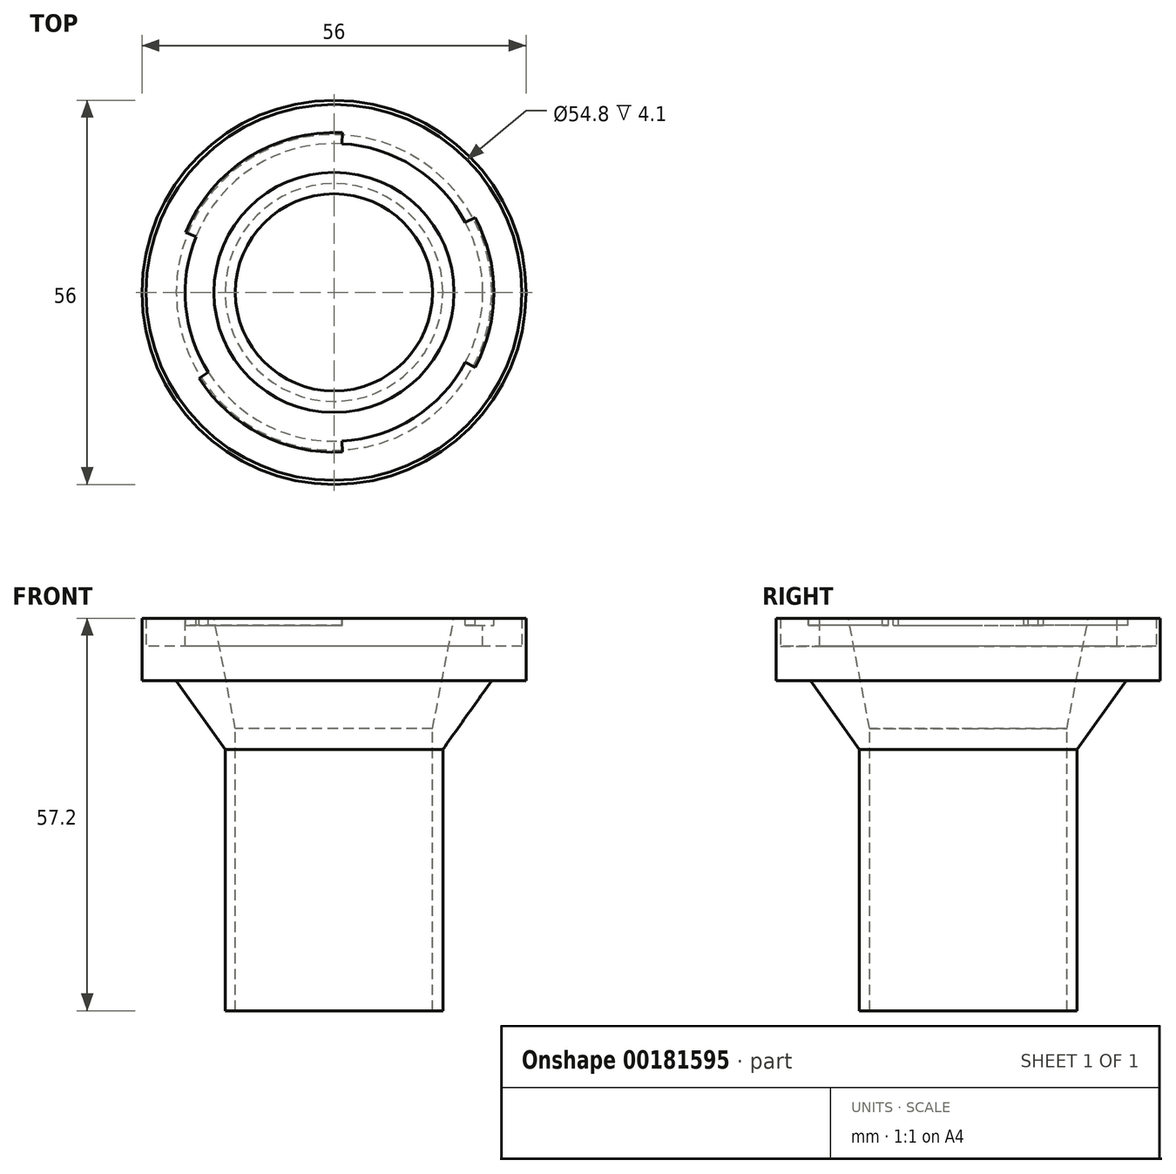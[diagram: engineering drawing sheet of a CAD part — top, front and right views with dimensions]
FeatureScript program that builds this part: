
annotation { "Feature Type Name" : "Feature", "Feature Type Description" : "" }
export const myFeature = defineFeature(function(context is Context, id is Id, definition is map)
    precondition{}
    {
        {
            var Q0;
            Q0=qCreatedBy(makeId("Front.planeOp"),FACE);
            var sketch = newSketch(context, id + "F0", { "sketchPlane" : qUnion([Q0])});
            skLineSegment(sketch, "E0", {"start": v(-17.5, 0) * mm, "end": v(-23.3, 0) * mm});
            skLineSegment(sketch, "E1", {"start": v(-23.3, 0) * mm, "end": v(-23.3, -1) * mm});
            skLineSegment(sketch, "E2", {"start": v(-23.3, -1) * mm, "end": v(-21.7, -1) * mm});
            skLineSegment(sketch, "E3", {"start": v(-21.7, -1) * mm, "end": v(-21.7, -4.1) * mm});
            skLineSegment(sketch, "E4", {"start": v(-21.7, -4.1) * mm, "end": v(-28, -4.1) * mm});
            skLineSegment(sketch, "E5", {"start": v(-28, -4.1) * mm, "end": v(-28, -9.1) * mm});
            skLineSegment(sketch, "E6", {"start": v(-28, -9.1) * mm, "end": v(-23, -9.1) * mm});
            skLineSegment(sketch, "E7", {"start": v(-23, -9.1) * mm, "end": v(-15.88, -19.1) * mm});
            skLineSegment(sketch, "E8", {"start": v(-15.88, -19.1) * mm, "end": v(-15.87, -57.2) * mm});
            skLineSegment(sketch, "E9", {"start": v(-15.87, -57.2) * mm, "end": v(-14.37, -57.2) * mm});
            skLineSegment(sketch, "E10", {"start": v(-14.37, -57.2) * mm, "end": v(-14.37, -16.1) * mm});
            skLineSegment(sketch, "E11", {"start": v(-14.37, -16.1) * mm, "end": v(-17.5, 0) * mm});
            skLineSegment(sketch, "E12", {"start": v(0, 0) * mm, "end": v(0, -57.2) * mm, "construction": true});
            skSolve(sketch);
        }
        {
            var Q0;
            Q0 = qSketchRegion(id + "F0", true);
            var Q1;
            Q1=sQuery(id+"F0.wireOp",EDGE,"E12");
            revolve(context, id + "F1", {"entities" : qUnion([Q0]), "axis" : qUnion([Q1]), "revolveType" : RevolveType.FULL});
        }
        {
            var Q0;
            Q0=makeQuery(id+"F1.opRevolve","SWEPT_FACE",FACE,{"disambiguationData":[OSD([sQuery(id+"F0.wireOp",EDGE,"E0")])]});
            var sketch = newSketch(context, id + "F2", { "sketchPlane" : qUnion([Q0])});
            skLineSegment(sketch, "E13", {"start": v(0, 0) * mm, "end": v(28, 0) * mm, "construction": true});
            skLineSegment(sketch, "E14", {"start": v(1.22, -23.27) * mm, "end": v(0, 0) * mm, "construction": true});
            skLineSegment(sketch, "E15", {"start": v(-19.65, -12.52) * mm, "end": v(0, 0) * mm, "construction": true});
            skLineSegment(sketch, "E16", {"start": v(-21.6, 8.73) * mm, "end": v(0, 0) * mm, "construction": true});
            skLineSegment(sketch, "E17", {"start": v(1.22, 23.27) * mm, "end": v(0, 0) * mm, "construction": true});
            skLineSegment(sketch, "E18", {"start": v(20.57, 10.94) * mm, "end": v(0, 0) * mm, "construction": true});
            skLineSegment(sketch, "E19", {"start": v(20.57, -10.94) * mm, "end": v(0, 0) * mm, "construction": true});
            skCircle(sketch, "E20", {"center": v(0, 0) * mm, "radius": 21.7 * mm, "construction": true});
            skLineSegment(sketch, "E21", {"start": v(20.57, -10.94) * mm, "end": v(19.16, -10.19) * mm});
            skLineSegment(sketch, "E22", {"start": v(20.57, 10.94) * mm, "end": v(19.16, 10.19) * mm});
            skLineSegment(sketch, "E23", {"start": v(1.22, 23.27) * mm, "end": v(1.14, 21.67) * mm});
            skLineSegment(sketch, "E24", {"start": v(-21.6, 8.73) * mm, "end": v(-20.12, 8.13) * mm});
            skLineSegment(sketch, "E25", {"start": v(-19.65, -12.52) * mm, "end": v(-18.3, -11.66) * mm});
            skLineSegment(sketch, "E26", {"start": v(1.22, -23.27) * mm, "end": v(1.14, -21.67) * mm});
            skArc(sketch, "E27", {"start": v(19.16, -10.19) * mm, "mid": v(11.66, -18.3) * mm, "end": v(1.14, -21.67) * mm});
            skArc(sketch, "E28", {"start": v(20.57, -10.94) * mm, "mid": v(12.52, -19.65) * mm, "end": v(1.22, -23.27) * mm});
            skArc(sketch, "E29", {"start": v(-18.3, -11.66) * mm, "mid": v(-21.6, -1.99) * mm, "end": v(-20.12, 8.13) * mm});
            skArc(sketch, "E30", {"start": v(-19.65, -12.52) * mm, "mid": v(-23.2, -2.13) * mm, "end": v(-21.6, 8.73) * mm});
            skArc(sketch, "E31", {"start": v(1.14, 21.67) * mm, "mid": v(11.66, 18.3) * mm, "end": v(19.16, 10.19) * mm});
            skArc(sketch, "E32", {"start": v(1.22, 23.27) * mm, "mid": v(12.52, 19.65) * mm, "end": v(20.57, 10.94) * mm});
            skLineSegment(sketch, "E33", {"start": v(0, 0) * mm, "end": v(0, 23.3) * mm, "construction": true});
            skSolve(sketch);
        }
        {
            var Q0;
            Q0 = qSketchRegion(id + "F2", true);
            var Q1;
            Q1=makeQuery(id+"F1.opRevolve","SWEPT_FACE",FACE,{"disambiguationData":[OSD([sQuery(id+"F0.wireOp",EDGE,"E2")])]});
            extrude(context, id + "F3", {"entities" : qUnion([Q0]), "operationType" : NewBodyOperationType.REMOVE, "endBound" : BoundingType.UP_TO_SURFACE, "oppositeDirection" : true, "endBoundEntityFace" : qUnion([Q1]), "depth" : 25 * mm});
        }
        {
            var Q0;
            Q0=makeQuery(id+"F1.opRevolve","SWEPT_FACE",FACE,{"disambiguationData":[OSD([sQuery(id+"F0.wireOp",EDGE,"E4")])]});
            var sketch = newSketch(context, id + "F4", { "sketchPlane" : qUnion([Q0])});
            skCircle(sketch, "E34.0", {"center": v(0, 0) * mm, "radius": 28 * mm});
            skCircle(sketch, "E35", {"center": v(0, 0) * mm, "radius": 27.4 * mm});
            skSolve(sketch);
        }
        {
            var Q0;
            Q0 = qSketchRegion(id + "F4", true);
            var Q1;
            Q1=makeQuery(id+"F1.opRevolve","SWEPT_FACE",FACE,{"disambiguationData":[OSD([sQuery(id+"F0.wireOp",EDGE,"E0")])]});
            extrude(context, id + "F5", {"entities" : qUnion([Q0]), "operationType" : NewBodyOperationType.ADD, "endBound" : BoundingType.UP_TO_SURFACE, "endBoundEntityFace" : qUnion([Q1]), "depth" : 25 * mm});
        }
    });
